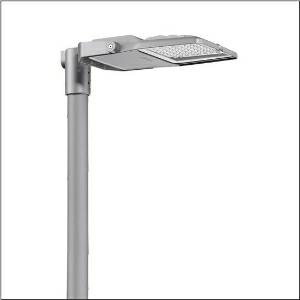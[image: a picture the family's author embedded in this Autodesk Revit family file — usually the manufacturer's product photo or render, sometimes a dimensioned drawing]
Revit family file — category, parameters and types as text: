
# Revit family: floodlight_fl_21_mini___pl61_5xa7772c4c3a_41e9
name_source: partatom
category: Lighting Fixtures
units: mm (PartAtom-declared; Revit-internal decimal feet)

## family parameters
Cut with Voids When Loaded = No
Host = Face
Light Source = No
Part Type = Normal
Room Calculation Point = No
Round Connector Dimension = Use Diameter
Shared = No

## types (1)
- --- (1 x LED, 12490 lm, 87.2 W, 4000K)
    Apparent Load = 87 VA
    CIE Flux Codes = 33 65 98 100 100
    Color Rendering = 70
    Color Temperature = 4000K
    Default Elevation = 1800 mm
    Description = Floodlight FL 21 mini, floodlight, primary light control with lens, of PMMA, primary optical cover: protective disc, of toughened safety glass, transparent, light distribution: PL61, light emission: direct distribution, installation type: surface-mounted, LED, High Power LED, rated luminous flux: 12.490lm, luminous efficacy: 143lm/W, light colour: 740, colour temperature: 4000K, control gear: ECG iQ, control: Auto-Match, Temp-Guard, Night-Set, Smart-Wire, Desk-Remote (wireless, voltage-free reading and setting of iQ features in the workshop via application-optimized NFC function/RFID function), optimised constant luminous flux control (CLO 2.0), Light-Fading, Lumen-Switch, with terminal, 6-pole, mains connection: 220..240V, AC, 50/60Hz, start of lifetime: 87W, end of lifetime: 92W, reduction: 40W, luminaire housing, of diecast aluminium, powder-coated, Siteco® metallic grey (DB 702S), corrosivity category C5 according to DIN EN ISO 12944, mast bracket, of steel, galvanised, powder-coated, protection rating (complete): IP66, insulation class (complete): insulation class II (safety insulation), certification: CE, ENEC, VDE, protection symbol: D, impact resistance: IK08, permissible operating ambient temperature: -40..+40°C, permissible operating ambient temperature for outdoor applications: -40..+50°C, standard: DIN EN 12944, packaging unit: 1 piece

Light Distribution: PL61
    Height = 70 mm
    Lamp = 1 x LED
    Lamp Light Flux = 12490 lm
    Lamp Power = 87.2 W
    Lamp count = 1
    Length = 485 mm
    Luminous efficacy = 143 lm/W
    Manufacturer = Siteco
    ModVariant = No
    Model = 5XA7772C4C3A
    Number of Poles = 1
    OnlyDefault = Yes
    Power Factor = 1
    Product Name = Floodlight FL 21 mini | PL61
    Product group = floodlight | pylon top
    ProductGroupID = 6101
    Protection Class = Protection class II
    Protection Degree = IP 66
    RLX_Detail_Level = 1
    RlxData = <blob elided: 101261 chars, md5=62cbeebf>
    Socket = socket
    Standby Power = 0 W
    System Light Flux = 12490 lm
    System Power = 87 W
    Type Comments = factory setting: luminous flux: 100 % | dim-lin: 254 | 456 mA
    Type Image = l_1007125.jpg
    URL = http://relux.com
    VarID = @adj_085225
    Voltage = 0 V
    Weight = 0.00 kg
    Width = 337 mm

## geometry (parser evidence)
native form markers: Blend x4, Sweep x12
no freeform markers — native parametric forms only
